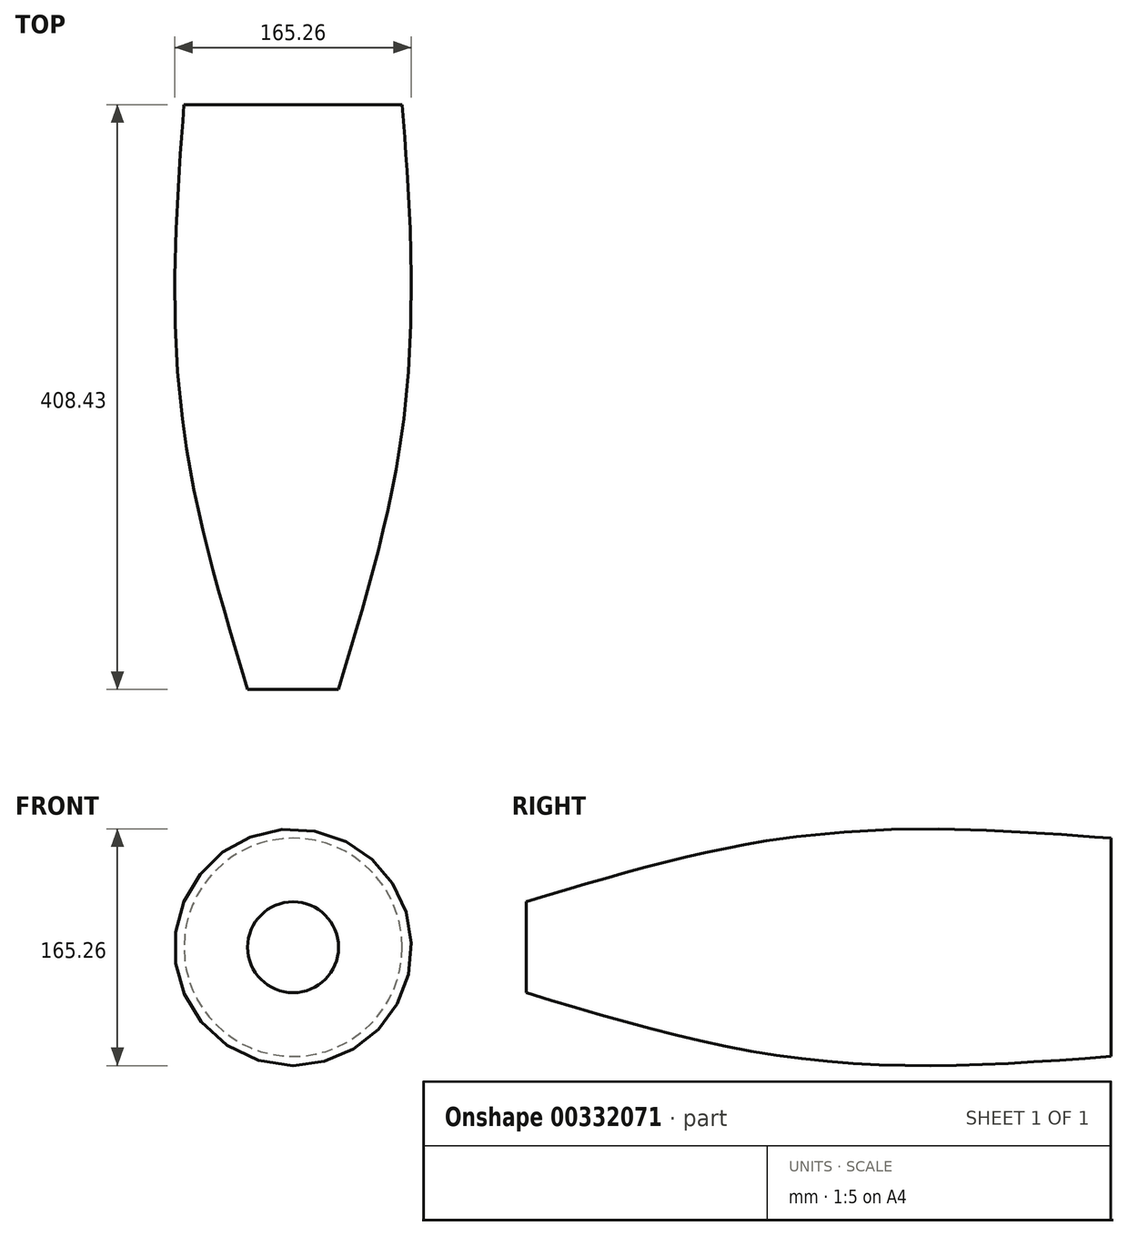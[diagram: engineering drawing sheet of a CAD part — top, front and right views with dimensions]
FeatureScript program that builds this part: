
annotation { "Feature Type Name" : "Feature", "Feature Type Description" : "" }
export const myFeature = defineFeature(function(context is Context, id is Id, definition is map)
    precondition{}
    {
        {
            var Q0;
            Q0=qCreatedBy(makeId("Front.planeOp"),FACE);
            cPlane(context, id + "F0", {"entities" : qUnion([Q0]), "cplaneType" : CPlaneType.OFFSET, "offset" : 116.33 * mm, "width" : 152.4 * mm, "height" : 152.4 * mm});
        }
        {
            var Q0;
            Q0=qCreatedBy(id+"F0.planeOp",FACE);
            cPlane(context, id + "F1", {"entities" : qUnion([Q0]), "cplaneType" : CPlaneType.OFFSET, "offset" : 111.76 * mm, "width" : 152.4 * mm, "height" : 152.4 * mm});
        }
        {
            var Q0;
            Q0=qCreatedBy(id+"F1.planeOp",FACE);
            cPlane(context, id + "F2", {"entities" : qUnion([Q0]), "cplaneType" : CPlaneType.OFFSET, "offset" : 180.34 * mm, "width" : 152.4 * mm, "height" : 152.4 * mm});
        }
        {
            var Q0;
            Q0=qCreatedBy(makeId("Front.planeOp"),FACE);
            var sketch = newSketch(context, id + "F3", { "sketchPlane" : qUnion([Q0])});
            skCircle(sketch, "E0", {"center": v(0, 0) * mm, "radius": 76.2 * mm});
            skSolve(sketch);
        }
        {
            var Q0;
            Q0=qCreatedBy(id+"F0.planeOp",FACE);
            var sketch = newSketch(context, id + "F4", { "sketchPlane" : qUnion([Q0])});
            skCircle(sketch, "E1", {"center": v(0, 0) * mm, "radius": 82.55 * mm});
            skSolve(sketch);
        }
        {
            var Q0;
            Q0=qCreatedBy(id+"F1.planeOp",FACE);
            var sketch = newSketch(context, id + "F5", { "sketchPlane" : qUnion([Q0])});
            skCircle(sketch, "E2", {"center": v(0, 0) * mm, "radius": 76.2 * mm});
            skSolve(sketch);
        }
        {
            var Q0;
            Q0=qCreatedBy(id+"F2.planeOp",FACE);
            var sketch = newSketch(context, id + "F6", { "sketchPlane" : qUnion([Q0])});
            skCircle(sketch, "E3", {"center": v(0, 0) * mm, "radius": 31.75 * mm});
            skSolve(sketch);
        }
        {
            var Q0;
            Q0=makeQuery(id+"F3.imprint","IMPRINT",FACE,{"disambiguationData":[TD([[makeQuery(id+"F3.imprint","IMPRINT",EDGE,{"derivedFrom":sQuery(id+"F3.wireOp",EDGE,"E0")}),1.0]])]});
            var Q1;
            Q1=makeQuery(id+"F4.imprint","IMPRINT",FACE,{"disambiguationData":[TD([[makeQuery(id+"F4.imprint","IMPRINT",EDGE,{"derivedFrom":sQuery(id+"F4.wireOp",EDGE,"E1")}),1.0]])]});
            var Q2;
            Q2=makeQuery(id+"F5.imprint","IMPRINT",FACE,{"disambiguationData":[TD([[makeQuery(id+"F5.imprint","IMPRINT",EDGE,{"derivedFrom":sQuery(id+"F5.wireOp",EDGE,"E2")}),1.0]])]});
            var Q3;
            Q3=makeQuery(id+"F6.imprint","IMPRINT",FACE,{"disambiguationData":[TD([[makeQuery(id+"F6.imprint","IMPRINT",EDGE,{"derivedFrom":sQuery(id+"F6.wireOp",EDGE,"E3")}),1.0]])]});
            loft(context, id + "F7", {"sheetProfilesArray" : [{ "sheetProfileEntities" : qUnion([Q0]) }, { "sheetProfileEntities" : qUnion([Q1]) }, { "sheetProfileEntities" : qUnion([Q2]) }, { "sheetProfileEntities" : qUnion([Q3]) }]});
        }
    });
